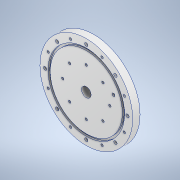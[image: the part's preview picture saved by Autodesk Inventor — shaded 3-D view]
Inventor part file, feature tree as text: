
AUTODESK INVENTOR PART (.ipt)
format: ipt  version: 2021 (Build 250183000, 183)  size: 202,752 bytes
history: native  units: mm
features: sketch x7, extrude x5, pattern_circular x3, hole x2
ambient origin geometry x8: Origin, YZ Plane, XZ Plane, XY Plane, X Axis, Y Axis, Z Axis, Center Point
bodies: Solid1 (feature_tree)
feature tree (17):
  extrude  "Extrusion1"  Depth=10.0mm TaperAngle=0.0deg
  extrude  "Extrusion3"  Depth=4.4mm
  extrude  "Extrusion2"  Depth=10.0mm TaperAngle=360.0deg
  pattern_circular  "Circular Pattern1"  Count=8 Angle=360.0deg
  hole  "Hole1"  [1 undecoded]
  pattern_circular  "Circular Pattern2"  Angle=45.0deg  [1 undecoded]
  extrude  "Extrusion4"  TaperAngle=22.5deg  [1 undecoded]
  extrude  "Extrusion5"  Depth=8.0mm
  hole  "Hole2"  [1 undecoded]
  pattern_circular  "Circular Pattern3"  [2 undecoded]
  sketch  "Sketch1"  dims[d0=126.0mm d1=10.0mm d2=0.0mm]
  sketch  "Sketch2"  dims[d3=112.0mm d4=4.4mm]
  sketch  "Sketch3"  dims[d5=10.0mm d6=0.0mm d7=80.0mm d8=360.0deg]
  sketch  "Sketch4"  dims[d11=3.0mm]
  sketch  "Sketch5"  dims[d12=2.5mm d13=0.0mm]
  sketch  "Sketch6"  dims[d14=64.0mm]
  sketch  "Sketch7"  dims[d15=3.242mm d16=6.0mm d17=4.0mm d18=2.0mm d19=90.0deg d20=8.0mm d21=0.0mm d22=80.0mm d23=360.0deg d25=4.0mm d26=45.0deg d27=22.5deg d29=84.0mm d30=0.0mm d31=0.0mm d32=13.0mm d33=0.0mm d34=0.0mm d35=98.0mm d36=45.0deg d37=22.5deg d38=3.242mm d39=8.0mm d40=8.0mm d41=4.0mm d42=90.0deg d43=8.0mm d44=20.594885mm d45=80.0mm d46=360.0deg]
note: 6 required parameter values undecoded (feature->parameter linkage not recoverable at this tier; creation-order binding heuristic only, values carry confidence <= 0.55)
